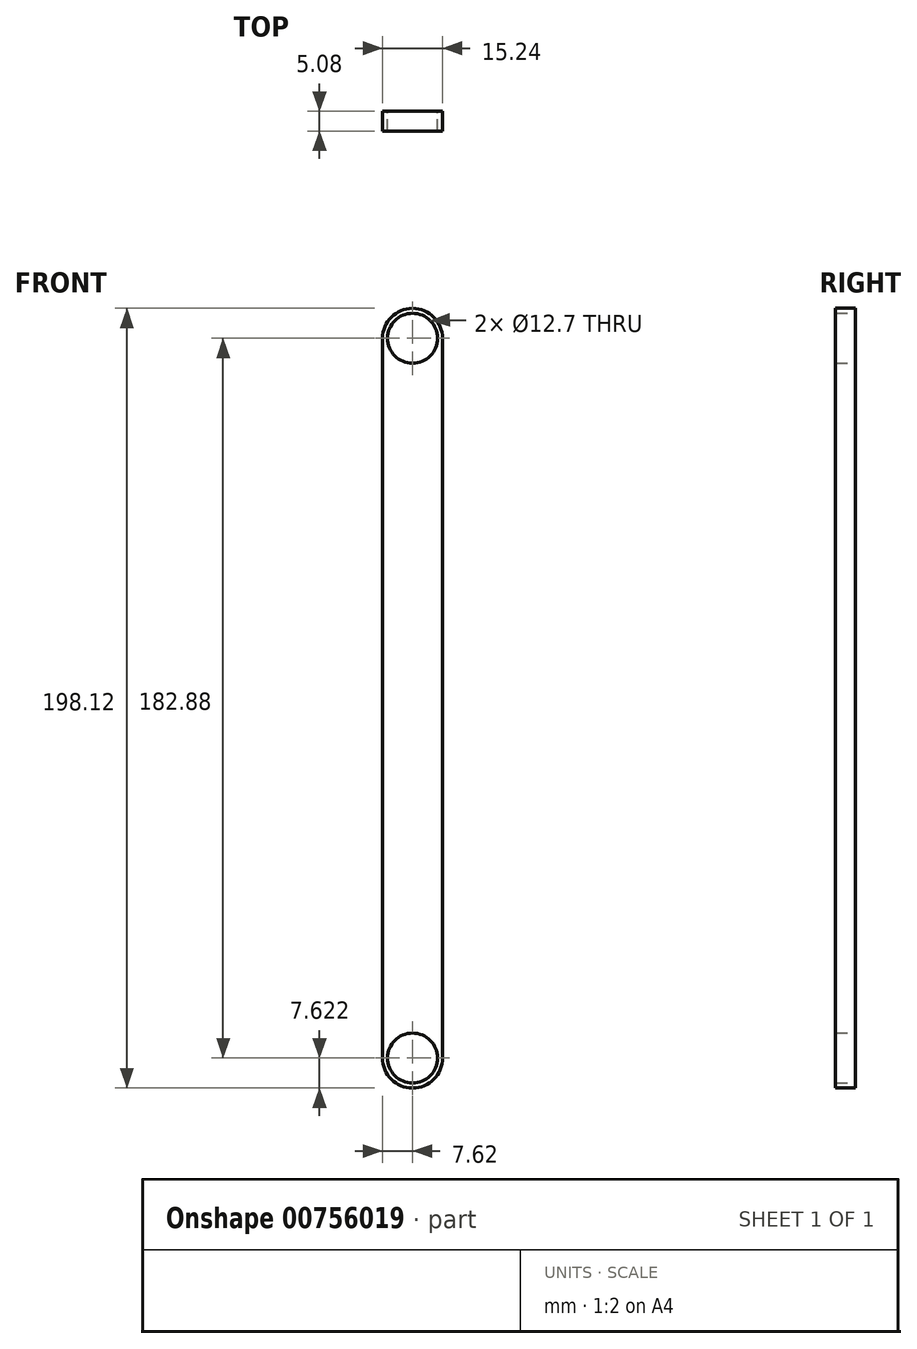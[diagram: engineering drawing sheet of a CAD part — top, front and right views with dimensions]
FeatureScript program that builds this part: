
annotation { "Feature Type Name" : "Feature", "Feature Type Description" : "" }
export const myFeature = defineFeature(function(context is Context, id is Id, definition is map)
    precondition{}
    {
        {
            var Q0;
            Q0=qCreatedBy(makeId("Front.planeOp"),FACE);
            var sketch = newSketch(context, id + "F0", { "sketchPlane" : qUnion([Q0])});
            skCircle(sketch, "E0", {"center": v(0, 162.23) * mm, "radius": 6.35 * mm});
            skCircle(sketch, "E1", {"center": v(0, -20.65) * mm, "radius": 6.35 * mm});
            skLineSegment(sketch, "E2", {"start": v(0, 162.23) * mm, "end": v(0, -20.65) * mm, "construction": true});
            skCircle(sketch, "E3", {"center": v(0, 162.23) * mm, "radius": 7.62 * mm});
            skCircle(sketch, "E4", {"center": v(0, -20.65) * mm, "radius": 7.62 * mm});
            skLineSegment(sketch, "E5", {"start": v(7.62, 162.23) * mm, "end": v(7.62, -20.65) * mm});
            skLineSegment(sketch, "E6.MirrorCS", {"start": v(-7.62, 162.23) * mm, "end": v(-7.62, -20.65) * mm});
            skSolve(sketch);
        }
        {
            var Q0;
            {var subQ0=sQuery(id+"F0.wireOp",EDGE,"E5");Q0=makeQuery(id+"F0.imprint","IMPRINT",FACE,{"disambiguationData":[TD([[makeQuery(id+"F0.imprint","IMPRINT",EDGE,{"derivedFrom":subQ0}),-1.0]])]});}
            var Q1;
            Q1=makeQuery(id+"F0.imprint","IMPRINT",FACE,{"disambiguationData":[TD([[makeQuery(id+"F0.imprint","IMPRINT",EDGE,{"derivedFrom":sQuery(id+"F0.wireOp",EDGE,"E1")}),-1.0]])]});
            var Q2;
            Q2=makeQuery(id+"F0.imprint","IMPRINT",FACE,{"disambiguationData":[TD([[makeQuery(id+"F0.imprint","IMPRINT",EDGE,{"derivedFrom":sQuery(id+"F0.wireOp",EDGE,"E0")}),-1.0]])]});
            extrude(context, id + "F1", {"entities" : qUnion([Q0, Q1, Q2]), "depth" : 5.08 * mm, "offsetDistance" : 25.4 * mm});
        }
    });
